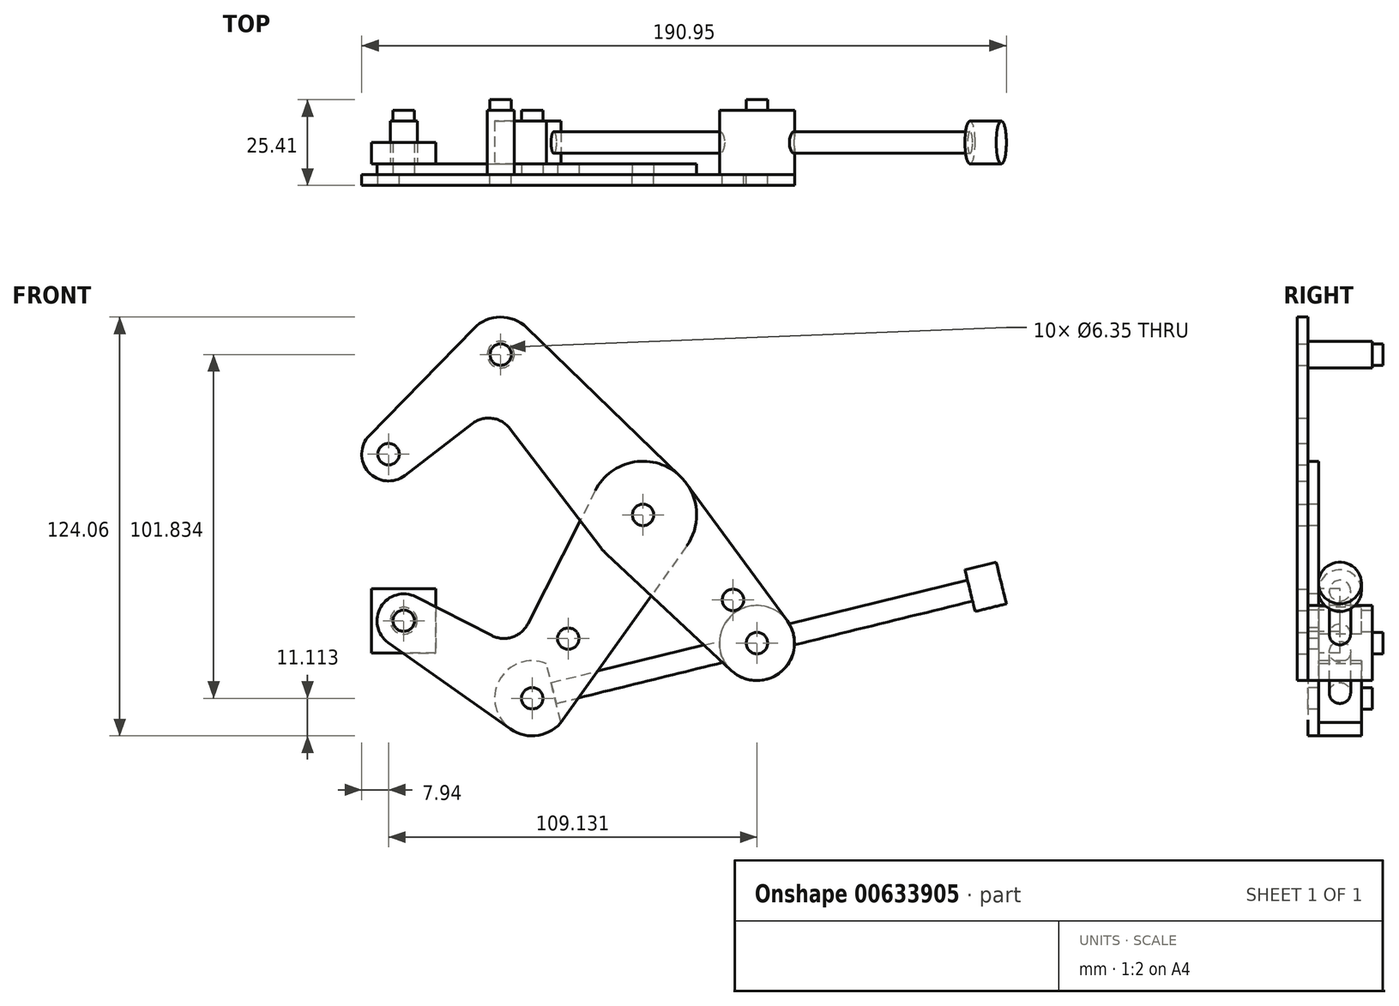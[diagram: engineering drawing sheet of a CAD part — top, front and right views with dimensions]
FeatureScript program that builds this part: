
annotation { "Feature Type Name" : "Feature", "Feature Type Description" : "" }
export const myFeature = defineFeature(function(context is Context, id is Id, definition is map)
    precondition{}
    {
        {
            var Q0;
            Q0=qCreatedBy(makeId("Front.planeOp"),FACE);
            var sketch = newSketch(context, id + "F0", { "sketchPlane" : qUnion([Q0])});
            skCircle(sketch, "E0", {"center": v(-64.57, 13.24) * mm, "radius": 7.94 * mm});
            skLineSegment(sketch, "E1", {"start": v(-64.57, 13.24) * mm, "end": v(-31.33, 42.76) * mm, "construction": true});
            skLineSegment(sketch, "E2", {"start": v(-31.33, 42.76) * mm, "end": v(10.83, -4.72) * mm, "construction": true});
            skLineSegment(sketch, "E3", {"start": v(10.83, -4.72) * mm, "end": v(44.56, -42.7) * mm, "construction": true});
            skCircle(sketch, "E4", {"center": v(10.83, -4.72) * mm, "radius": 15.88 * mm});
            skCircle(sketch, "E5", {"center": v(44.56, -42.7) * mm, "radius": 11.11 * mm});
            skCircle(sketch, "E6", {"center": v(-31.33, 42.76) * mm, "radius": 11.11 * mm});
            skCircle(sketch, "E7", {"center": v(10.83, -4.72) * mm, "radius": 3.98 * mm});
            skLineSegment(sketch, "E8", {"start": v(10.83, -4.72) * mm, "end": v(-22, -59.08) * mm, "construction": true});
            skLineSegment(sketch, "E9", {"start": v(-22, -59.08) * mm, "end": v(-60.05, -36.1) * mm, "construction": true});
            skCircle(sketch, "E10", {"center": v(-60.05, -36.1) * mm, "radius": 7.94 * mm});
            skCircle(sketch, "E11", {"center": v(-22, -59.08) * mm, "radius": 11.11 * mm});
            skLineSegment(sketch, "E12", {"start": v(-22, -59.08) * mm, "end": v(-11.33, -41.4) * mm, "construction": true});
            skCircle(sketch, "E13", {"center": v(-11.33, -41.4) * mm, "radius": 3.18 * mm});
            skLineSegment(sketch, "E14", {"start": v(10.83, -4.72) * mm, "end": v(35.08, -32.04) * mm, "construction": true});
            skLineSegment(sketch, "E15", {"start": v(35.08, -32.04) * mm, "end": v(37.46, -29.93) * mm, "construction": true});
            skCircle(sketch, "E16", {"center": v(37.46, -29.93) * mm, "radius": 3.17 * mm});
            skCircle(sketch, "E17", {"center": v(44.56, -42.7) * mm, "radius": 3.18 * mm});
            skCircle(sketch, "E18", {"center": v(-31.33, 42.76) * mm, "radius": 3.18 * mm});
            skCircle(sketch, "E19", {"center": v(10.83, -4.72) * mm, "radius": 3.18 * mm});
            skCircle(sketch, "E20", {"center": v(-64.57, 13.24) * mm, "radius": 3.18 * mm});
            skCircle(sketch, "E21", {"center": v(-60.05, -36.1) * mm, "radius": 3.18 * mm});
            skCircle(sketch, "E22", {"center": v(-22, -59.08) * mm, "radius": 3.18 * mm});
            skLineSegment(sketch, "E23", {"start": v(-70.25, 18.79) * mm, "end": v(-39.29, 50.52) * mm});
            skLineSegment(sketch, "E24", {"start": v(-59.74, 6.95) * mm, "end": v(-39.74, 22.3) * mm});
            skLineSegment(sketch, "E25", {"start": v(-23.6, 50.74) * mm, "end": v(21.88, 6.68) * mm});
            skLineSegment(sketch, "E26", {"start": v(-28.58, 20.8) * mm, "end": v(-1.8, -14.35) * mm});
            skPoint(sketch, "E27", {"position": v(-33.41, 27.15) * mm});
            skLineSegment(sketch, "E28", {"start": v(23.64, 4.66) * mm, "end": v(53.52, -36.14) * mm});
            skLineSegment(sketch, "E29", {"start": v(0, -16.33) * mm, "end": v(36.98, -50.83) * mm});
            skLineSegment(sketch, "E30", {"start": v(23.76, -13.93) * mm, "end": v(-12.95, -65.52) * mm});
            skLineSegment(sketch, "E31", {"start": v(-64.63, -42.58) * mm, "end": v(-28.42, -68.15) * mm});
            skLineSegment(sketch, "E32", {"start": v(-56.44, -29.02) * mm, "end": v(-34, -40.48) * mm});
            skLineSegment(sketch, "E33", {"start": v(-3.34, 2.44) * mm, "end": v(-23.28, -36.99) * mm});
            skPoint(sketch, "E34", {"position": v(-26.89, -44.1) * mm});
            skArc(sketch, "E35.filletArc", {"start": v(-28.58, 20.8) * mm, "mid": v(-33.85, 23.87) * mm, "end": v(-39.74, 22.3) * mm});
            skArc(sketch, "E36.filletArc", {"start": v(-34, -40.48) * mm, "mid": v(-27.91, -40.96) * mm, "end": v(-23.28, -36.99) * mm});
            skSolve(sketch);
        }
        {
            var Q0;
            Q0=makeQuery(id+"F0.imprint","IMPRINT",FACE,{"disambiguationData":[TD([[makeQuery(id+"F0.imprint","IMPRINT",EDGE,{"derivedFrom":sQuery(id+"F0.wireOp",EDGE,"E13")}),-1.0]])]});
            var Q1;
            {var subQ0=sQuery(id+"F0.wireOp",EDGE,"E26");var subQ1=sQuery(id+"F0.wireOp",EDGE,"E4");var subQ2=makeQuery(id+"F0.imprint","INTERSECT",VERTEX,{"derivedFrom":[subQ1,subQ0]});Q1=makeQuery(id+"F0.imprint","IMPRINT",FACE,{"disambiguationData":[TD([[makeQuery(id+"F0.imprint","IMPRINT",EDGE,{"disambiguationData":[TD([[subQ2,1.0]])],"derivedFrom":subQ1}),-1.0]])]});}
            var Q2;
            Q2=makeQuery(id+"F0.imprint","IMPRINT",FACE,{"disambiguationData":[TD([[makeQuery(id+"F0.imprint","IMPRINT",EDGE,{"derivedFrom":sQuery(id+"F0.wireOp",EDGE,"E7")}),-1.0]])]});
            var Q3;
            {var subQ0=sQuery(id+"F0.wireOp",EDGE,"E29");var subQ1=sQuery(id+"F0.wireOp",EDGE,"E4");var subQ2=makeQuery(id+"F0.imprint","INTERSECT",VERTEX,{"derivedFrom":[subQ1,subQ0]});Q3=makeQuery(id+"F0.imprint","IMPRINT",FACE,{"disambiguationData":[TD([[makeQuery(id+"F0.imprint","IMPRINT",EDGE,{"disambiguationData":[TD([[subQ2,-1.0]])],"derivedFrom":subQ1}),-1.0]])]});}
            var Q4;
            Q4=makeQuery(id+"F0.imprint","IMPRINT",FACE,{"disambiguationData":[TD([[makeQuery(id+"F0.imprint","IMPRINT",EDGE,{"derivedFrom":sQuery(id+"F0.wireOp",EDGE,"E21")}),-1.0]])]});
            var Q5;
            Q5=makeQuery(id+"F0.imprint","IMPRINT",FACE,{"disambiguationData":[TD([[makeQuery(id+"F0.imprint","IMPRINT",EDGE,{"derivedFrom":sQuery(id+"F0.wireOp",EDGE,"E22")}),-1.0]])]});
            var Q6;
            Q6=makeQuery(id+"F0.imprint","IMPRINT",FACE,{"disambiguationData":[TD([[makeQuery(id+"F0.imprint","IMPRINT",EDGE,{"derivedFrom":sQuery(id+"F0.wireOp",EDGE,"E7")}),1.0]])]});
            extrude(context, id + "F1", {"entities" : qUnion([Q0, Q1, Q2, Q3, Q4, Q5, Q6]), "oppositeDirection" : true, "depth" : 3.17 * mm, "offsetDistance" : 25.4 * mm});
        }
        {
            var Q0;
            {var subQ0=sQuery(id+"F0.wireOp",EDGE,"E23");Q0=makeQuery(id+"F0.imprint","IMPRINT",FACE,{"disambiguationData":[TD([[makeQuery(id+"F0.imprint","IMPRINT",EDGE,{"derivedFrom":subQ0}),-1.0]])]});}
            var Q1;
            Q1=makeQuery(id+"F0.imprint","IMPRINT",FACE,{"disambiguationData":[TD([[makeQuery(id+"F0.imprint","IMPRINT",EDGE,{"derivedFrom":sQuery(id+"F0.wireOp",EDGE,"E20")}),-1.0]])]});
            var Q2;
            Q2=makeQuery(id+"F0.imprint","IMPRINT",FACE,{"disambiguationData":[TD([[makeQuery(id+"F0.imprint","IMPRINT",EDGE,{"derivedFrom":sQuery(id+"F0.wireOp",EDGE,"E18")}),-1.0]])]});
            var Q3;
            Q3=makeQuery(id+"F0.imprint","IMPRINT",FACE,{"disambiguationData":[TD([[makeQuery(id+"F0.imprint","IMPRINT",EDGE,{"derivedFrom":sQuery(id+"F0.wireOp",EDGE,"E7")}),-1.0]])]});
            var Q4;
            {var subQ0=sQuery(id+"F0.wireOp",EDGE,"E26");var subQ1=sQuery(id+"F0.wireOp",EDGE,"E4");var subQ2=makeQuery(id+"F0.imprint","INTERSECT",VERTEX,{"derivedFrom":[subQ1,subQ0]});Q4=makeQuery(id+"F0.imprint","IMPRINT",FACE,{"disambiguationData":[TD([[makeQuery(id+"F0.imprint","IMPRINT",EDGE,{"disambiguationData":[TD([[subQ2,1.0]])],"derivedFrom":subQ1}),-1.0]])]});}
            var Q5;
            {var subQ0=sQuery(id+"F0.wireOp",EDGE,"E29");var subQ1=sQuery(id+"F0.wireOp",EDGE,"E4");var subQ2=makeQuery(id+"F0.imprint","INTERSECT",VERTEX,{"derivedFrom":[subQ1,subQ0]});Q5=makeQuery(id+"F0.imprint","IMPRINT",FACE,{"disambiguationData":[TD([[makeQuery(id+"F0.imprint","IMPRINT",EDGE,{"disambiguationData":[TD([[subQ2,-1.0]])],"derivedFrom":subQ1}),-1.0]])]});}
            var Q6;
            Q6=makeQuery(id+"F0.imprint","IMPRINT",FACE,{"disambiguationData":[TD([[makeQuery(id+"F0.imprint","IMPRINT",EDGE,{"derivedFrom":sQuery(id+"F0.wireOp",EDGE,"E7")}),1.0]])]});
            var Q7;
            Q7=makeQuery(id+"F0.imprint","IMPRINT",FACE,{"disambiguationData":[TD([[makeQuery(id+"F0.imprint","IMPRINT",EDGE,{"derivedFrom":sQuery(id+"F0.wireOp",EDGE,"E16")}),-1.0]])]});
            var Q8;
            Q8=makeQuery(id+"F0.imprint","IMPRINT",FACE,{"disambiguationData":[TD([[makeQuery(id+"F0.imprint","IMPRINT",EDGE,{"derivedFrom":sQuery(id+"F0.wireOp",EDGE,"E17")}),-1.0]])]});
            extrude(context, id + "F2", {"entities" : qUnion([Q0, Q1, Q2, Q3, Q4, Q5, Q6, Q7, Q8]), "depth" : 3.17 * mm, "offsetDistance" : 25.4 * mm});
        }
        {
            var Q0;
            Q0=makeQuery(id+"F2.opExtrude","CAP_FACE",FACE,{"disambiguationData":[OSD([sQuery(id+"F0.wireOp",EDGE,"E0"),sQuery(id+"F0.wireOp",EDGE,"E4"),sQuery(id+"F0.wireOp",EDGE,"E5"),sQuery(id+"F0.wireOp",EDGE,"E6"),sQuery(id+"F0.wireOp",EDGE,"E16"),sQuery(id+"F0.wireOp",EDGE,"E17"),sQuery(id+"F0.wireOp",EDGE,"E18"),sQuery(id+"F0.wireOp",EDGE,"E19"),sQuery(id+"F0.wireOp",EDGE,"E20"),sQuery(id+"F0.wireOp",EDGE,"E23"),sQuery(id+"F0.wireOp",EDGE,"E24"),sQuery(id+"F0.wireOp",EDGE,"E25"),sQuery(id+"F0.wireOp",EDGE,"E26"),sQuery(id+"F0.wireOp",EDGE,"E28"),sQuery(id+"F0.wireOp",EDGE,"E29"),sQuery(id+"F0.wireOp",EDGE,"E35.filletArc")])],"isStart":false});
            var sketch = newSketch(context, id + "F3", { "sketchPlane" : qUnion([Q0])});
            skCircle(sketch, "E37", {"center": v(-31.33, 42.76) * mm, "radius": 3.98 * mm});
            skCircle(sketch, "E38", {"center": v(10.83, -4.72) * mm, "radius": 3.98 * mm});
            skCircle(sketch, "E39", {"center": v(44.56, -42.7) * mm, "radius": 11.11 * mm});
            skSolve(sketch);
        }
        {
            var Q0;
            Q0=qCreatedBy(makeId("Front.planeOp"),FACE);
            var sketch = newSketch(context, id + "F4", { "sketchPlane" : qUnion([Q0])});
            skCircle(sketch, "E40", {"center": v(-60.05, -36.1) * mm, "radius": 3.98 * mm});
            skCircle(sketch, "E41", {"center": v(-22, -59.08) * mm, "radius": 11.11 * mm});
            skLineSegment(sketch, "E42", {"start": v(-15.65, -57.52) * mm, "end": v(44.56, -42.7) * mm, "construction": true});
            skLineSegment(sketch, "E43", {"start": v(-22, -59.08) * mm, "end": v(-15.65, -57.52) * mm, "construction": true});
            skLineSegment(sketch, "E44", {"start": v(-15.65, -57.52) * mm, "end": v(-17.8, -48.8) * mm});
            skLineSegment(sketch, "E45", {"start": v(-15.65, -57.52) * mm, "end": v(-13.5, -66.24) * mm});
            skPoint(sketch, "E46", {"position": v(44.56, -42.7) * mm});
            skSolve(sketch);
        }
        {
            var Q0;
            Q0=qCreatedBy(makeId("Front.planeOp"),FACE);
            cPlane(context, id + "F5", {"entities" : qUnion([Q0]), "cplaneType" : CPlaneType.OFFSET, "offset" : 9.52 * mm, "oppositeDirection" : true, "width" : 152.4 * mm, "height" : 152.4 * mm});
        }
        {
            var Q0;
            Q0=makeQuery(id+"F3.imprint","IMPRINT",FACE,{"disambiguationData":[TD([[makeQuery(id+"F3.imprint","IMPRINT",EDGE,{"derivedFrom":makeQuery(id+"F2.opExtrude","CAP_EDGE",EDGE,{"disambiguationData":[OSD([sQuery(id+"F0.wireOp",EDGE,"E17")])],"isStart":false})}),-1.0]])]});
            var Q1;
            Q1=makeQuery(id+"F3.imprint","IMPRINT",FACE,{"disambiguationData":[TD([[makeQuery(id+"F3.imprint","IMPRINT",EDGE,{"derivedFrom":sQuery(id+"F3.wireOp",EDGE,"E37")}),1.0]])]});
            var Q2;
            Q2=makeQuery(id+"F3.imprint","IMPRINT",FACE,{"disambiguationData":[TD([[makeQuery(id+"F3.imprint","IMPRINT",EDGE,{"derivedFrom":makeQuery(id+"F2.opExtrude","CAP_EDGE",EDGE,{"disambiguationData":[OSD([sQuery(id+"F0.wireOp",EDGE,"E18")])],"isStart":false})}),1.0]])]});
            var Q3;
            Q3=makeQuery(id+"F3.imprint","IMPRINT",FACE,{"disambiguationData":[TD([[makeQuery(id+"F3.imprint","IMPRINT",EDGE,{"derivedFrom":makeQuery(id+"F2.opExtrude","CAP_EDGE",EDGE,{"disambiguationData":[OSD([sQuery(id+"F0.wireOp",EDGE,"E17")])],"isStart":false})}),1.0]])]});
            var Q4;
            Q4=makeQuery(id+"F4.imprint","IMPRINT",FACE,{"disambiguationData":[TD([[makeQuery(id+"F4.imprint","IMPRINT",EDGE,{"derivedFrom":makeQuery(id+"F1.opExtrude","CAP_EDGE",EDGE,{"disambiguationData":[OSD([sQuery(id+"F0.wireOp",EDGE,"E21")])],"isStart":true})}),1.0]])]});
            var Q5;
            Q5=makeQuery(id+"F4.imprint","IMPRINT",FACE,{"disambiguationData":[TD([[makeQuery(id+"F4.imprint","IMPRINT",EDGE,{"derivedFrom":sQuery(id+"F4.wireOp",EDGE,"E40")}),1.0]])]});
            var Q6;
            {var subQ0=sQuery(id+"F4.wireOp",EDGE,"E44");Q6=makeQuery(id+"F4.imprint","IMPRINT",FACE,{"disambiguationData":[TD([[makeQuery(id+"F4.imprint","IMPRINT",EDGE,{"derivedFrom":subQ0}),1.0]])]});}
            var Q7;
            Q7=makeQuery(id+"F4.imprint","IMPRINT",FACE,{"disambiguationData":[TD([[makeQuery(id+"F4.imprint","IMPRINT",EDGE,{"derivedFrom":makeQuery(id+"F1.opExtrude","CAP_EDGE",EDGE,{"disambiguationData":[OSD([sQuery(id+"F0.wireOp",EDGE,"E22")])],"isStart":true})}),1.0]])]});
            var Q8;
            Q8=qCreatedBy(id+"F5.planeOp",FACE);
            extrude(context, id + "F6", {"entities" : qUnion([Q0, Q1, Q2, Q3, Q4, Q5, Q6, Q7]), "endBound" : BoundingType.UP_TO_SURFACE, "oppositeDirection" : true, "depth" : 25.4 * mm, "endBoundEntityFace" : qUnion([Q8]), "offsetDistance" : 25.4 * mm});
        }
        {
            var Q0;
            Q0=makeQuery(id+"F2.opExtrude","SWEPT_BODY",BODY,{"disambiguationData":[OSD([sQuery(id+"F0.wireOp",EDGE,"E0"),sQuery(id+"F0.wireOp",EDGE,"E4"),sQuery(id+"F0.wireOp",EDGE,"E5"),sQuery(id+"F0.wireOp",EDGE,"E6"),sQuery(id+"F0.wireOp",EDGE,"E16"),sQuery(id+"F0.wireOp",EDGE,"E17"),sQuery(id+"F0.wireOp",EDGE,"E18"),sQuery(id+"F0.wireOp",EDGE,"E19"),sQuery(id+"F0.wireOp",EDGE,"E20"),sQuery(id+"F0.wireOp",EDGE,"E23"),sQuery(id+"F0.wireOp",EDGE,"E24"),sQuery(id+"F0.wireOp",EDGE,"E25"),sQuery(id+"F0.wireOp",EDGE,"E26"),sQuery(id+"F0.wireOp",EDGE,"E28"),sQuery(id+"F0.wireOp",EDGE,"E29"),sQuery(id+"F0.wireOp",EDGE,"E35.filletArc")])]});
            var Q1;
            Q1=makeQuery(id+"F6.opExtrude","SWEPT_BODY",BODY,{"disambiguationData":[OSD([sQuery(id+"F3.wireOp",EDGE,"E39")])]});
            var Q2;
            Q2=makeQuery(id+"F6.opExtrude","SWEPT_BODY",BODY,{"disambiguationData":[OSD([sQuery(id+"F3.wireOp",EDGE,"E37")])]});
            booleanBodies(context, id + "F7", {"operationType" : BooleanOperationType.SUBTRACTION, "tools" : qUnion([Q0]), "targets" : qUnion([Q1, Q2]), "keepTools" : true});
        }
        {
            var Q0;
            Q0=makeQuery(id+"F1.opExtrude","SWEPT_BODY",BODY,{"disambiguationData":[OSD([sQuery(id+"F0.wireOp",EDGE,"E4"),sQuery(id+"F0.wireOp",EDGE,"E10"),sQuery(id+"F0.wireOp",EDGE,"E11"),sQuery(id+"F0.wireOp",EDGE,"E13"),sQuery(id+"F0.wireOp",EDGE,"E19"),sQuery(id+"F0.wireOp",EDGE,"E21"),sQuery(id+"F0.wireOp",EDGE,"E22"),sQuery(id+"F0.wireOp",EDGE,"E30"),sQuery(id+"F0.wireOp",EDGE,"E31"),sQuery(id+"F0.wireOp",EDGE,"E32"),sQuery(id+"F0.wireOp",EDGE,"E33"),sQuery(id+"F0.wireOp",EDGE,"E36.filletArc")])]});
            var Q1;
            Q1=makeQuery(id+"F6.opExtrude","SWEPT_BODY",BODY,{"disambiguationData":[OSD([sQuery(id+"F4.wireOp",EDGE,"E41"),sQuery(id+"F4.wireOp",EDGE,"E44"),sQuery(id+"F4.wireOp",EDGE,"E45")])]});
            var Q2;
            Q2=makeQuery(id+"F6.opExtrude","SWEPT_BODY",BODY,{"disambiguationData":[OSD([sQuery(id+"F4.wireOp",EDGE,"E40")])]});
            booleanBodies(context, id + "F8", {"operationType" : BooleanOperationType.SUBTRACTION, "tools" : qUnion([Q0]), "targets" : qUnion([Q1, Q2]), "keepTools" : true});
        }
        {
            var Q0;
            Q0=makeQuery(id+"F6.opExtrude","SWEPT_BODY",BODY,{"disambiguationData":[OSD([sQuery(id+"F3.wireOp",EDGE,"E37")])]});
            var Q1;
            Q1=makeQuery(id+"F6.opExtrude","SWEPT_BODY",BODY,{"disambiguationData":[OSD([sQuery(id+"F3.wireOp",EDGE,"E39")])]});
            var Q2;
            Q2=makeQuery(id+"F6.opExtrude","SWEPT_BODY",BODY,{"disambiguationData":[OSD([sQuery(id+"F4.wireOp",EDGE,"E41"),sQuery(id+"F4.wireOp",EDGE,"E44"),sQuery(id+"F4.wireOp",EDGE,"E45")])]});
            var Q3;
            Q3=makeQuery(id+"F6.opExtrude","SWEPT_BODY",BODY,{"disambiguationData":[OSD([sQuery(id+"F4.wireOp",EDGE,"E40")])]});
            var Q4;
            Q4=qCreatedBy(id+"F5.planeOp",FACE);
            mirror(context, id + "F9", {"entities" : qUnion([Q0, Q1, Q2, Q3]), "mirrorPlane" : qUnion([Q4])});
        }
        {
            var Q0;
            Q0=makeQuery(id+"F6.opExtrude","SWEPT_BODY",BODY,{"disambiguationData":[OSD([sQuery(id+"F3.wireOp",EDGE,"E37")])]});
            var Q1;
            Q1=makeQuery(id+"F9.opPattern","COPY",BODY,{"derivedFrom":makeQuery(id+"F6.opExtrude","SWEPT_BODY",BODY,{"disambiguationData":[OSD([sQuery(id+"F3.wireOp",EDGE,"E37")])]}),"instanceName":"1"});
            var Q2;
            Q2=makeQuery(id+"F6.opExtrude","SWEPT_BODY",BODY,{"disambiguationData":[OSD([sQuery(id+"F3.wireOp",EDGE,"E39")])]});
            var Q3;
            Q3=makeQuery(id+"F6.opExtrude","SWEPT_BODY",BODY,{"disambiguationData":[OSD([sQuery(id+"F4.wireOp",EDGE,"E40")])]});
            var Q4;
            Q4=makeQuery(id+"F6.opExtrude","SWEPT_BODY",BODY,{"disambiguationData":[OSD([sQuery(id+"F4.wireOp",EDGE,"E41"),sQuery(id+"F4.wireOp",EDGE,"E44"),sQuery(id+"F4.wireOp",EDGE,"E45")])]});
            var Q5;
            Q5=makeQuery(id+"F9.opPattern","COPY",BODY,{"derivedFrom":makeQuery(id+"F6.opExtrude","SWEPT_BODY",BODY,{"disambiguationData":[OSD([sQuery(id+"F3.wireOp",EDGE,"E39")])]}),"instanceName":"1"});
            var Q6;
            Q6=makeQuery(id+"F9.opPattern","COPY",BODY,{"derivedFrom":makeQuery(id+"F6.opExtrude","SWEPT_BODY",BODY,{"disambiguationData":[OSD([sQuery(id+"F4.wireOp",EDGE,"E40")])]}),"instanceName":"1"});
            var Q7;
            Q7=makeQuery(id+"F9.opPattern","COPY",BODY,{"derivedFrom":makeQuery(id+"F6.opExtrude","SWEPT_BODY",BODY,{"disambiguationData":[OSD([sQuery(id+"F4.wireOp",EDGE,"E41"),sQuery(id+"F4.wireOp",EDGE,"E44"),sQuery(id+"F4.wireOp",EDGE,"E45")])]}),"instanceName":"1"});
            booleanBodies(context, id + "F10", {"operationType" : BooleanOperationType.UNION, "tools" : qUnion([Q0, Q1, Q2, Q3, Q4, Q5, Q6, Q7])});
        }
        {
            var Q0;
            {var subQ0=makeQuery(id+"F6.opExtrude","SWEPT_FACE",FACE,{"disambiguationData":[OSD([sQuery(id+"F4.wireOp",EDGE,"E44"),sQuery(id+"F4.wireOp",EDGE,"E45")])]});Q0=makeQuery(id+"F10.opBoolean","MERGE",FACE,{"derivedFrom":[subQ0,makeQuery(id+"F9.opPattern","COPY",FACE,{"derivedFrom":subQ0,"instanceName":"1"})]});}
            var sketch = newSketch(context, id + "F11", { "sketchPlane" : qUnion([Q0])});
            skLineSegment(sketch, "E47", {"start": v(9.53, -61.1) * mm, "end": v(9.53, -43.13) * mm, "construction": true});
            skLineSegment(sketch, "E48", {"start": v(3.18, -52.11) * mm, "end": v(15.88, -52.11) * mm, "construction": true});
            skCircle(sketch, "E49", {"center": v(9.53, -52.11) * mm, "radius": 3.18 * mm});
            skSolve(sketch);
        }
        {
            var Q0;
            Q0=makeQuery(id+"F11.imprint","IMPRINT",FACE,{"disambiguationData":[TD([[makeQuery(id+"F11.imprint","IMPRINT",EDGE,{"derivedFrom":sQuery(id+"F11.wireOp",EDGE,"E49")}),1.0]])]});
            extrude(context, id + "F12", {"entities" : qUnion([Q0]), "oppositeDirection" : true, "depth" : 12.7 * mm, "offsetDistance" : 25.4 * mm});
        }
        {
            var Q0;
            Q0=makeQuery(id+"F12.opExtrude","CAP_FACE",FACE,{"disambiguationData":[OSD([sQuery(id+"F11.wireOp",EDGE,"E49")])],"isStart":true});
            extrude(context, id + "F13", {"entities" : qUnion([Q0]), "operationType" : NewBodyOperationType.ADD, "depth" : 127 * mm, "offsetDistance" : 25.4 * mm});
        }
        {
            var Q0;
            Q0=makeQuery(id+"F13.opExtrude","CAP_FACE",FACE,{"disambiguationData":[OSD([sQuery(id+"F11.wireOp",EDGE,"E49")])],"isStart":false});
            var sketch = newSketch(context, id + "F14", { "sketchPlane" : qUnion([Q0])});
            skCircle(sketch, "E50", {"center": v(9.53, -52.11) * mm, "radius": 6.35 * mm});
            skSolve(sketch);
        }
        {
            var Q0;
            Q0=makeQuery(id+"F14.imprint","IMPRINT",FACE,{"disambiguationData":[TD([[makeQuery(id+"F14.imprint","IMPRINT",EDGE,{"derivedFrom":sQuery(id+"F14.wireOp",EDGE,"E50")}),1.0]])]});
            var Q1;
            Q1=makeQuery(id+"F14.imprint","IMPRINT",FACE,{"disambiguationData":[TD([[makeQuery(id+"F14.imprint","IMPRINT",EDGE,{"derivedFrom":makeQuery(id+"F13.opExtrude","CAP_EDGE",EDGE,{"disambiguationData":[OSD([sQuery(id+"F11.wireOp",EDGE,"E49")])],"isStart":false})}),1.0]])]});
            extrude(context, id + "F15", {"entities" : qUnion([Q0, Q1]), "operationType" : NewBodyOperationType.ADD, "depth" : 9.52 * mm, "offsetDistance" : 25.4 * mm});
        }
        {
            var Q0;
            Q0=makeQuery(id+"F1.opExtrude","CAP_FACE",FACE,{"disambiguationData":[OSD([sQuery(id+"F0.wireOp",EDGE,"E4"),sQuery(id+"F0.wireOp",EDGE,"E10"),sQuery(id+"F0.wireOp",EDGE,"E11"),sQuery(id+"F0.wireOp",EDGE,"E13"),sQuery(id+"F0.wireOp",EDGE,"E19"),sQuery(id+"F0.wireOp",EDGE,"E21"),sQuery(id+"F0.wireOp",EDGE,"E22"),sQuery(id+"F0.wireOp",EDGE,"E30"),sQuery(id+"F0.wireOp",EDGE,"E31"),sQuery(id+"F0.wireOp",EDGE,"E32"),sQuery(id+"F0.wireOp",EDGE,"E33"),sQuery(id+"F0.wireOp",EDGE,"E36.filletArc")])],"isStart":false});
            var sketch = newSketch(context, id + "F16", { "sketchPlane" : qUnion([Q0])});
            skLineSegment(sketch, "E51.bottom", {"start": v(69.58, -26.57) * mm, "end": v(50.53, -26.57) * mm});
            skLineSegment(sketch, "E51.top", {"start": v(69.58, -45.62) * mm, "end": v(50.53, -45.62) * mm});
            skLineSegment(sketch, "E51.left", {"start": v(69.58, -26.57) * mm, "end": v(69.58, -45.62) * mm});
            skLineSegment(sketch, "E51.right", {"start": v(50.53, -26.57) * mm, "end": v(50.53, -45.62) * mm});
            skPoint(sketch, "E51.middle", {"position": v(60.05, -36.1) * mm});
            skLineSegment(sketch, "E52.bottom", {"start": v(74.1, 22.77) * mm, "end": v(55.05, 22.77) * mm});
            skLineSegment(sketch, "E52.top", {"start": v(74.1, 3.72) * mm, "end": v(55.05, 3.72) * mm});
            skLineSegment(sketch, "E52.left", {"start": v(74.1, 22.77) * mm, "end": v(74.1, 3.72) * mm});
            skLineSegment(sketch, "E52.right", {"start": v(55.05, 22.77) * mm, "end": v(55.05, 3.72) * mm});
            skPoint(sketch, "E52.middle", {"position": v(64.57, 13.24) * mm});
            skSolve(sketch);
        }
        {
            var Q0;
            {var subQ1=sQuery(id+"F16.wireOp",EDGE,"E51.bottom");Q0=makeQuery(id+"F16.imprint","IMPRINT",FACE,{"disambiguationData":[TD([[makeQuery(id+"F16.imprint","IMPRINT",EDGE,{"derivedFrom":subQ1}),1.0]])]});}
            var Q1;
            {var subQ5=makeQuery(id+"F1.opExtrude","CAP_EDGE",EDGE,{"disambiguationData":[OSD([sQuery(id+"F0.wireOp",EDGE,"E10")])],"isStart":false});Q1=makeQuery(id+"F16.imprint","IMPRINT",FACE,{"disambiguationData":[TD([[makeQuery(id+"F16.imprint","IMPRINT",EDGE,{"derivedFrom":subQ5}),-1.0]])]});}
            var Q2;
            Q2=qCreatedBy(id+"F5.planeOp",FACE);
            extrude(context, id + "F17", {"entities" : qUnion([Q0, Q1]), "endBound" : BoundingType.UP_TO_SURFACE, "depth" : 25.4 * mm, "endBoundEntityFace" : qUnion([Q2]), "offsetDistance" : 25.4 * mm});
        }
    });
